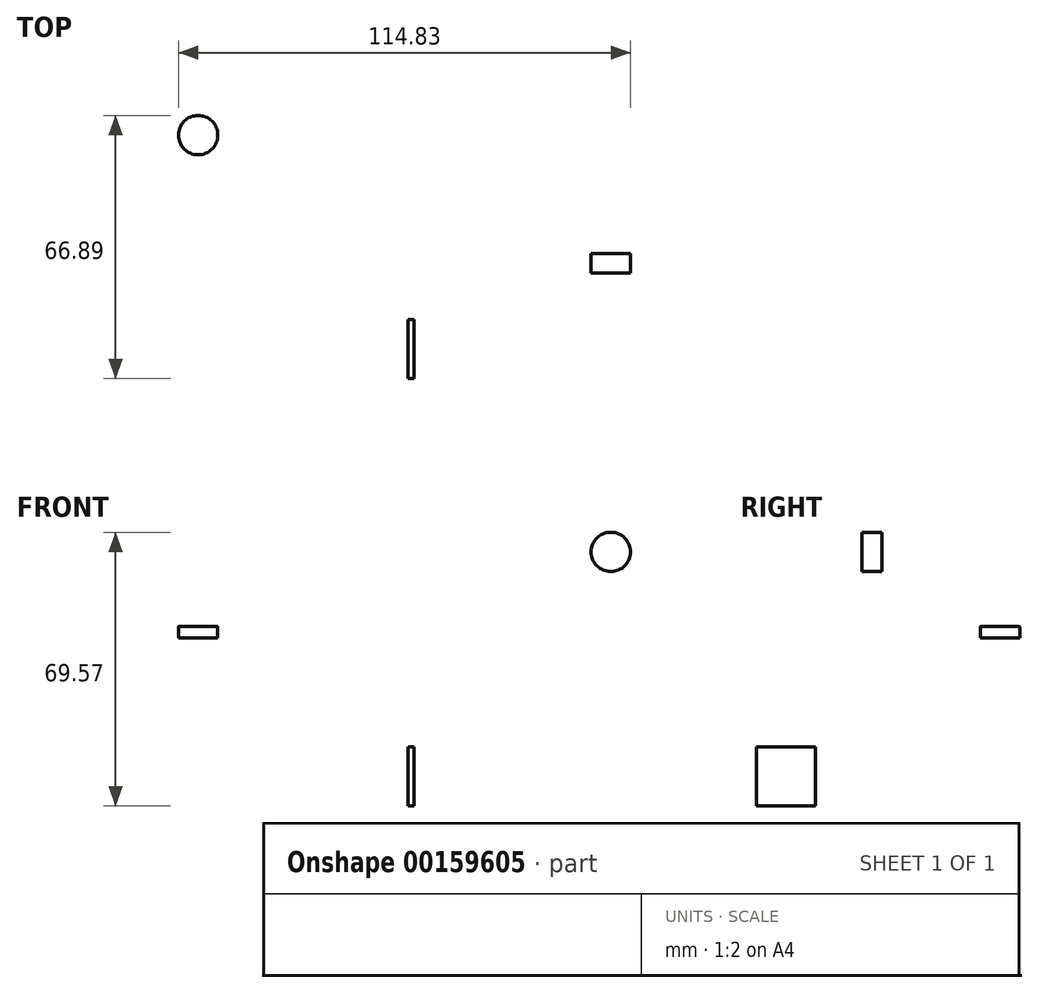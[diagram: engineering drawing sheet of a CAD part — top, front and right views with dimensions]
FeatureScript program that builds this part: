
annotation { "Feature Type Name" : "Feature", "Feature Type Description" : "" }
export const myFeature = defineFeature(function(context is Context, id is Id, definition is map)
    precondition{}
    {
        {
            assignVariable(context, id + "F0", {"name" : "W", "anyValue" : 1});
        }
        {
            var Q0;
            Q0=qCreatedBy(makeId("Top.planeOp"),FACE);
            var sketch = newSketch(context, id + "F1", { "sketchPlane" : qUnion([Q0])});
            skCircle(sketch, "E0", {"center": v(-53.28, 30.04) * mm, "radius": 5 * mm});
            skSolve(sketch);
        }
        {
            var Q0;
            Q0 = qSketchRegion(id + "F1", true);
            extrude(context, id + "F2", {"entities" : qUnion([Q0]), "depth" : (getVariable(context, 'W') * 3) * mm});
        }
        {
            var Q0;
            Q0=makeQuery(id+"F2.opExtrude","CAP_EDGE",EDGE,{"disambiguationData":[OSD([sQuery(id+"F1.wireOp",EDGE,"E0")])],"isStart":false});
            fillet(context, id + "F3", {"entities" : qUnion([Q0]), "radius" : (getVariable(context, 'W') * 1 / 5) * mm, "tangentPropagation" : true, "allowEdgeOverflow" : false});
        }
        {
            var Q0;
            Q0=qCreatedBy(makeId("Front.planeOp"),FACE);
            var sketch = newSketch(context, id + "F4", { "sketchPlane" : qUnion([Q0])});
            skCircle(sketch, "E1", {"center": v(51.55, 21.88) * mm, "radius": 5 * mm});
            skSolve(sketch);
        }
        {
            var Q0;
            Q0=makeQuery(id+"F4.imprint","IMPRINT",FACE,{"disambiguationData":[TD([[makeQuery(id+"F4.imprint","IMPRINT",EDGE,{"derivedFrom":sQuery(id+"F4.wireOp",EDGE,"E1")}),1.0]])]});
            extrude(context, id + "F5", {"entities" : qUnion([Q0]), "depth" : (getVariable(context, 'W') * 5) * mm});
        }
        {
            var Q0;
            Q0=qCreatedBy(makeId("Right.planeOp"),FACE);
            var sketch = newSketch(context, id + "F6", { "sketchPlane" : qUnion([Q0])});
            skLineSegment(sketch, "E2.bottom", {"start": v(-16.85, -27.69) * mm, "end": v(-31.85, -27.69) * mm});
            skLineSegment(sketch, "E2.top", {"start": v(-16.85, -42.69) * mm, "end": v(-31.85, -42.69) * mm});
            skLineSegment(sketch, "E2.left", {"start": v(-16.85, -27.69) * mm, "end": v(-16.85, -42.69) * mm});
            skLineSegment(sketch, "E2.right", {"start": v(-31.85, -27.69) * mm, "end": v(-31.85, -42.69) * mm});
            skSolve(sketch);
        }
        {
            var Q0;
            Q0=makeQuery(id+"F6.imprint","IMPRINT",FACE,{"disambiguationData":[TD([[makeQuery(id+"F6.imprint","IMPRINT",EDGE,{"derivedFrom":sQuery(id+"F6.wireOp",EDGE,"E2.bottom")}),1.0]])]});
            extrude(context, id + "F7", {"entities" : qUnion([Q0]), "depth" : (getVariable(context, 'W') * 1.5) * mm});
        }
    });
